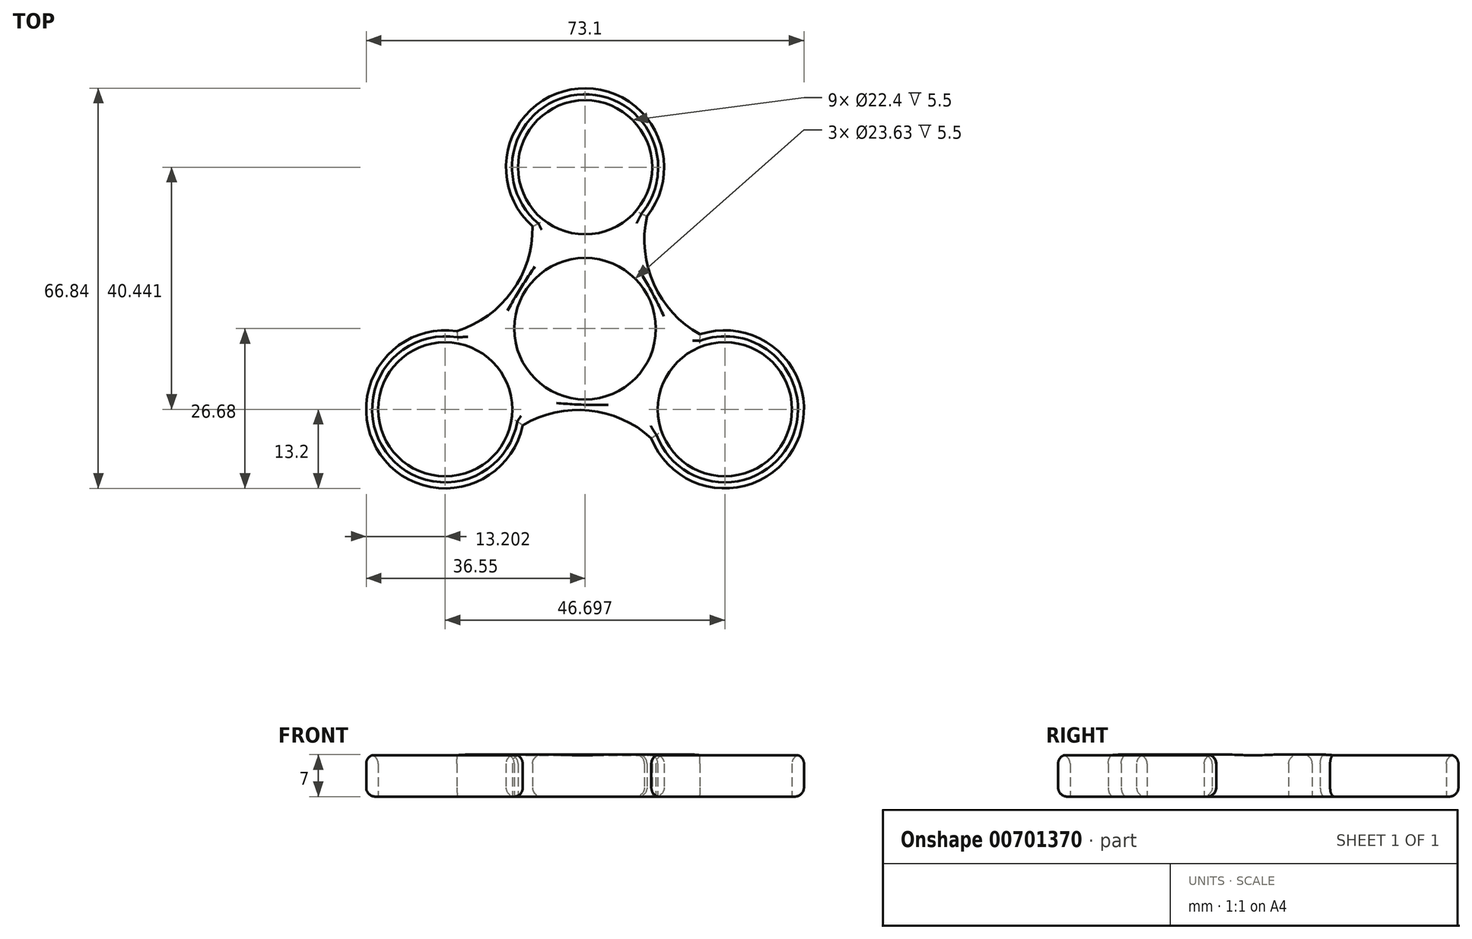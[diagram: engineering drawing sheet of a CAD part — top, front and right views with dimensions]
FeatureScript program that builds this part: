
annotation { "Feature Type Name" : "Feature", "Feature Type Description" : "" }
export const myFeature = defineFeature(function(context is Context, id is Id, definition is map)
    precondition{}
    {
        {
            var Q0;
            Q0=qCreatedBy(makeId("Top.planeOp"),FACE);
            var sketch = newSketch(context, id + "F0", { "sketchPlane" : qUnion([Q0])});
            skCircle(sketch, "E0", {"center": v(0, 0) * mm, "radius": 11.82 * mm});
            skCircle(sketch, "E1", {"center": v(0, 26.96) * mm, "radius": 11.2 * mm});
            skArc(sketch, "E2", {"start": v(10.33, 18.74) * mm, "mid": v(-1.13, 40.11) * mm, "end": v(-8.77, 17.1) * mm});
            skCircle(sketch, "E3.1.0", {"center": v(-23.35, -13.48) * mm, "radius": 11.2 * mm});
            skArc(sketch, "E3.1.1", {"start": v(-21.4, -0.43) * mm, "mid": v(-34.17, -21.03) * mm, "end": v(-10.42, -16.15) * mm});
            skCircle(sketch, "E3.2.0", {"center": v(23.35, -13.48) * mm, "radius": 11.2 * mm});
            skArc(sketch, "E3.2.1", {"start": v(11.06, -18.31) * mm, "mid": v(35.3, -19.08) * mm, "end": v(19.2, -0.95) * mm});
            skArc(sketch, "E4", {"start": v(10.33, 18.74) * mm, "mid": v(11.5, 7.43) * mm, "end": v(19.2, -0.95) * mm});
            skArc(sketch, "E5.1.0", {"start": v(-21.4, -0.43) * mm, "mid": v(-12.18, 6.25) * mm, "end": v(-8.77, 17.1) * mm});
            skArc(sketch, "E5.2.0", {"start": v(11.06, -18.31) * mm, "mid": v(0.68, -13.68) * mm, "end": v(-10.42, -16.15) * mm});
            skSolve(sketch);
        }
        {
            var Q0;
            Q0=makeQuery(id+"F0.imprint","IMPRINT",FACE,{"disambiguationData":[TD([[makeQuery(id+"F0.imprint","IMPRINT",EDGE,{"derivedFrom":sQuery(id+"F0.wireOp",EDGE,"E0")}),-1.0]])]});
            extrude(context, id + "F1", {"entities" : qUnion([Q0]), "depth" : 7 * mm, "offsetDistance" : 25 * mm});
        }
        {
            var Q0;
            Q0=makeQuery(id+"F1.opExtrude","CAP_EDGE",EDGE,{"disambiguationData":[OSD([sQuery(id+"F0.wireOp",EDGE,"E5.1.0")])],"isStart":false});
            var Q1;
            Q1=makeQuery(id+"F1.opExtrude","CAP_EDGE",EDGE,{"disambiguationData":[OSD([sQuery(id+"F0.wireOp",EDGE,"E3.1.0")])],"isStart":false});
            var Q2;
            Q2=makeQuery(id+"F1.opExtrude","CAP_EDGE",EDGE,{"disambiguationData":[OSD([sQuery(id+"F0.wireOp",EDGE,"E1")])],"isStart":false});
            var Q3;
            Q3=makeQuery(id+"F1.opExtrude","CAP_FACE",FACE,{"disambiguationData":[OSD([sQuery(id+"F0.wireOp",EDGE,"E0"),sQuery(id+"F0.wireOp",EDGE,"E1"),sQuery(id+"F0.wireOp",EDGE,"E2"),sQuery(id+"F0.wireOp",EDGE,"E3.1.0"),sQuery(id+"F0.wireOp",EDGE,"E3.1.1"),sQuery(id+"F0.wireOp",EDGE,"E3.2.0"),sQuery(id+"F0.wireOp",EDGE,"E3.2.1"),sQuery(id+"F0.wireOp",EDGE,"E4"),sQuery(id+"F0.wireOp",EDGE,"E5.1.0"),sQuery(id+"F0.wireOp",EDGE,"E5.2.0")])],"isStart":false});
            fillet(context, id + "F2", {"entities" : qUnion([Q0, Q1, Q2, Q3]), "radius" : 1.5 * mm, "tangentPropagation" : true, "allowEdgeOverflow" : false});
        }
        {
            var Q0;
            Q0=makeQuery(id+"F1.opExtrude","CAP_EDGE",EDGE,{"disambiguationData":[OSD([sQuery(id+"F0.wireOp",EDGE,"E3.2.1")])],"isStart":true});
            var Q1;
            Q1=makeQuery(id+"F1.opExtrude","CAP_EDGE",EDGE,{"disambiguationData":[OSD([sQuery(id+"F0.wireOp",EDGE,"E5.2.0")])],"isStart":true});
            var Q2;
            Q2=makeQuery(id+"F1.opExtrude","CAP_EDGE",EDGE,{"disambiguationData":[OSD([sQuery(id+"F0.wireOp",EDGE,"E3.1.1")])],"isStart":true});
            var Q3;
            Q3=makeQuery(id+"F1.opExtrude","CAP_EDGE",EDGE,{"disambiguationData":[OSD([sQuery(id+"F0.wireOp",EDGE,"E5.1.0")])],"isStart":true});
            var Q4;
            Q4=makeQuery(id+"F1.opExtrude","CAP_EDGE",EDGE,{"disambiguationData":[OSD([sQuery(id+"F0.wireOp",EDGE,"E4")])],"isStart":true});
            var Q5;
            Q5=makeQuery(id+"F1.opExtrude","CAP_EDGE",EDGE,{"disambiguationData":[OSD([sQuery(id+"F0.wireOp",EDGE,"E2")])],"isStart":true});
            fillet(context, id + "F3", {"entities" : qUnion([Q0, Q1, Q2, Q3, Q4, Q5]), "radius" : 1.5 * mm, "tangentPropagation" : true, "allowEdgeOverflow" : false});
        }
    });
